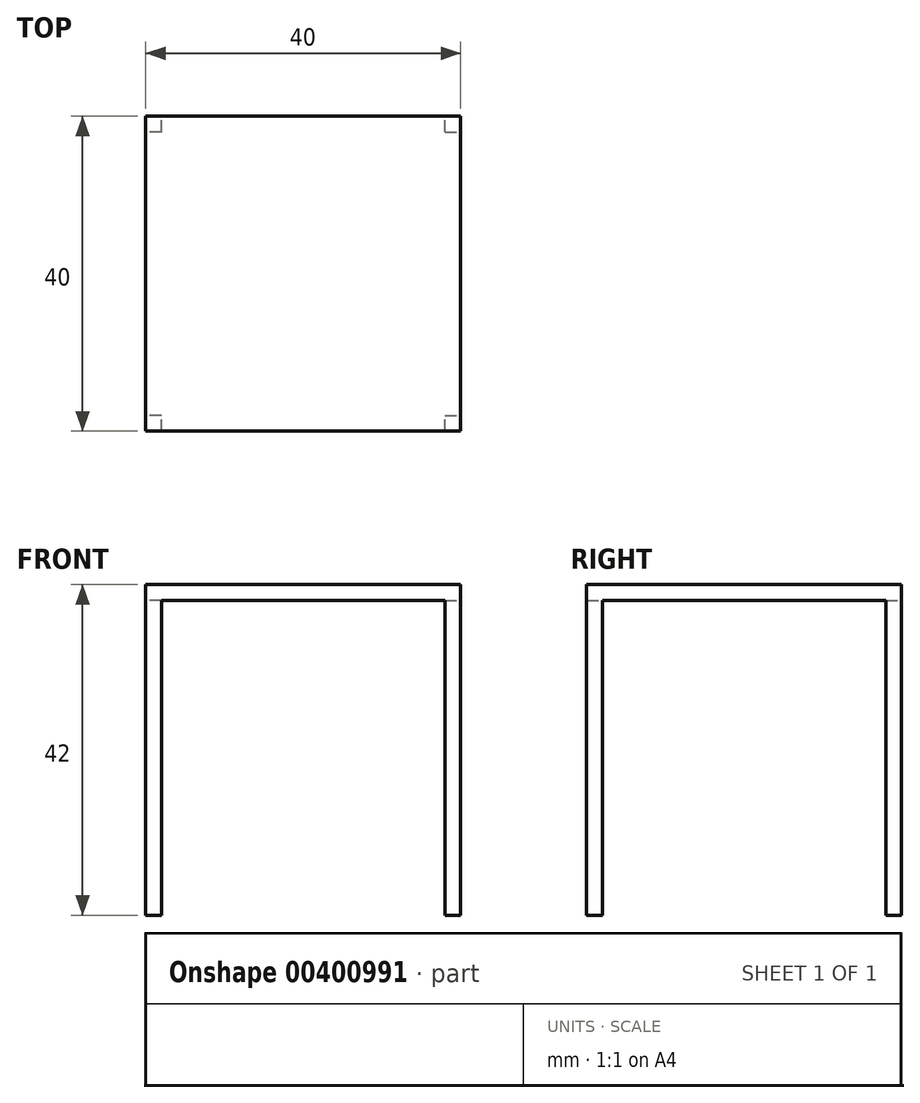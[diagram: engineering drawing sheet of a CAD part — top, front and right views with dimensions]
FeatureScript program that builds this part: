
annotation { "Feature Type Name" : "Feature", "Feature Type Description" : "" }
export const myFeature = defineFeature(function(context is Context, id is Id, definition is map)
    precondition{}
    {
        {
            var Q0;
            Q0=qCreatedBy(makeId("Top.planeOp"),FACE);
            var sketch = newSketch(context, id + "F0", { "sketchPlane" : qUnion([Q0])});
            skLineSegment(sketch, "E0.bottom", {"start": v(20, -20) * mm, "end": v(-20, -20) * mm});
            skLineSegment(sketch, "E0.top", {"start": v(20, 20) * mm, "end": v(-20, 20) * mm});
            skLineSegment(sketch, "E0.left", {"start": v(20, -20) * mm, "end": v(20, 20) * mm});
            skLineSegment(sketch, "E0.right", {"start": v(-20, -20) * mm, "end": v(-20, 20) * mm});
            skPoint(sketch, "E0.middle", {"position": v(0, 0) * mm});
            skSolve(sketch);
        }
        {
            var Q0;
            Q0=makeQuery(id+"F0.imprint","IMPRINT",FACE,{"disambiguationData":[TD([[makeQuery(id+"F0.imprint","IMPRINT",EDGE,{"derivedFrom":sQuery(id+"F0.wireOp",EDGE,"E0.bottom")}),-1.0]])]});
            extrude(context, id + "F1", {"entities" : qUnion([Q0]), "depth" : 2 * mm});
        }
        {
            var Q0;
            Q0=makeQuery(id+"F1.opExtrude","SWEPT_FACE",FACE,{"disambiguationData":[OSD([sQuery(id+"F0.wireOp",EDGE,"E0.left")])]});
            var sketch = newSketch(context, id + "F2", { "sketchPlane" : qUnion([Q0])});
            skLineSegment(sketch, "E1.bottom", {"start": v(-20, 0) * mm, "end": v(-18, 0) * mm});
            skLineSegment(sketch, "E1.top", {"start": v(-20, -40) * mm, "end": v(-18, -40) * mm});
            skLineSegment(sketch, "E1.left", {"start": v(-20, 0) * mm, "end": v(-20, -40) * mm});
            skLineSegment(sketch, "E1.right", {"start": v(-18, 0) * mm, "end": v(-18, -40) * mm});
            skLineSegment(sketch, "E2.MirrorCS", {"start": v(18, 0) * mm, "end": v(18, -40) * mm});
            skLineSegment(sketch, "E3.MirrorCS", {"start": v(20, 0) * mm, "end": v(20, -40) * mm});
            skLineSegment(sketch, "E4.MirrorCS", {"start": v(20, -40) * mm, "end": v(18, -40) * mm});
            skLineSegment(sketch, "E5.MirrorCS", {"start": v(20, 0) * mm, "end": v(18, 0) * mm});
            skSolve(sketch);
        }
        {
            var Q0;
            Q0=makeQuery(id+"F2.imprint","IMPRINT",FACE,{"disambiguationData":[TD([[makeQuery(id+"F2.imprint","IMPRINT",EDGE,{"derivedFrom":sQuery(id+"F2.wireOp",EDGE,"E2.MirrorCS")}),1.0]])]});
            var Q1;
            Q1=makeQuery(id+"F2.imprint","IMPRINT",FACE,{"disambiguationData":[TD([[makeQuery(id+"F2.imprint","IMPRINT",EDGE,{"derivedFrom":sQuery(id+"F2.wireOp",EDGE,"E1.bottom")}),-1.0]])]});
            extrude(context, id + "F3", {"entities" : qUnion([Q0, Q1]), "operationType" : NewBodyOperationType.ADD, "depth" : -2 * mm});
        }
        {
            var Q0;
            Q0=makeQuery(id+"F1.opExtrude","SWEPT_FACE",FACE,{"disambiguationData":[OSD([sQuery(id+"F0.wireOp",EDGE,"E0.right")])]});
            var sketch = newSketch(context, id + "F4", { "sketchPlane" : qUnion([Q0])});
            skLineSegment(sketch, "E6.bottom", {"start": v(-20, 0) * mm, "end": v(-18, 0) * mm});
            skLineSegment(sketch, "E6.top", {"start": v(-20, -40) * mm, "end": v(-18, -40) * mm});
            skLineSegment(sketch, "E6.left", {"start": v(-20, 0) * mm, "end": v(-20, -40) * mm});
            skLineSegment(sketch, "E6.right", {"start": v(-18, 0) * mm, "end": v(-18, -40) * mm});
            skLineSegment(sketch, "E7.MirrorCS", {"start": v(20, 0) * mm, "end": v(18, 0) * mm});
            skLineSegment(sketch, "E8.MirrorCS", {"start": v(20, 0) * mm, "end": v(20, -40) * mm});
            skLineSegment(sketch, "E9.MirrorCS", {"start": v(18, 0) * mm, "end": v(18, -40) * mm});
            skLineSegment(sketch, "E10.MirrorCS", {"start": v(20, -40) * mm, "end": v(18, -40) * mm});
            skSolve(sketch);
        }
        {
            var Q0;
            Q0=makeQuery(id+"F4.imprint","IMPRINT",FACE,{"disambiguationData":[TD([[makeQuery(id+"F4.imprint","IMPRINT",EDGE,{"derivedFrom":sQuery(id+"F4.wireOp",EDGE,"E6.bottom")}),1.0]])]});
            var Q1;
            Q1=makeQuery(id+"F4.imprint","IMPRINT",FACE,{"disambiguationData":[TD([[makeQuery(id+"F4.imprint","IMPRINT",EDGE,{"derivedFrom":sQuery(id+"F4.wireOp",EDGE,"E7.MirrorCS")}),1.0]])]});
            extrude(context, id + "F5", {"entities" : qUnion([Q0, Q1]), "operationType" : NewBodyOperationType.ADD, "depth" : -2 * mm});
        }
    });
